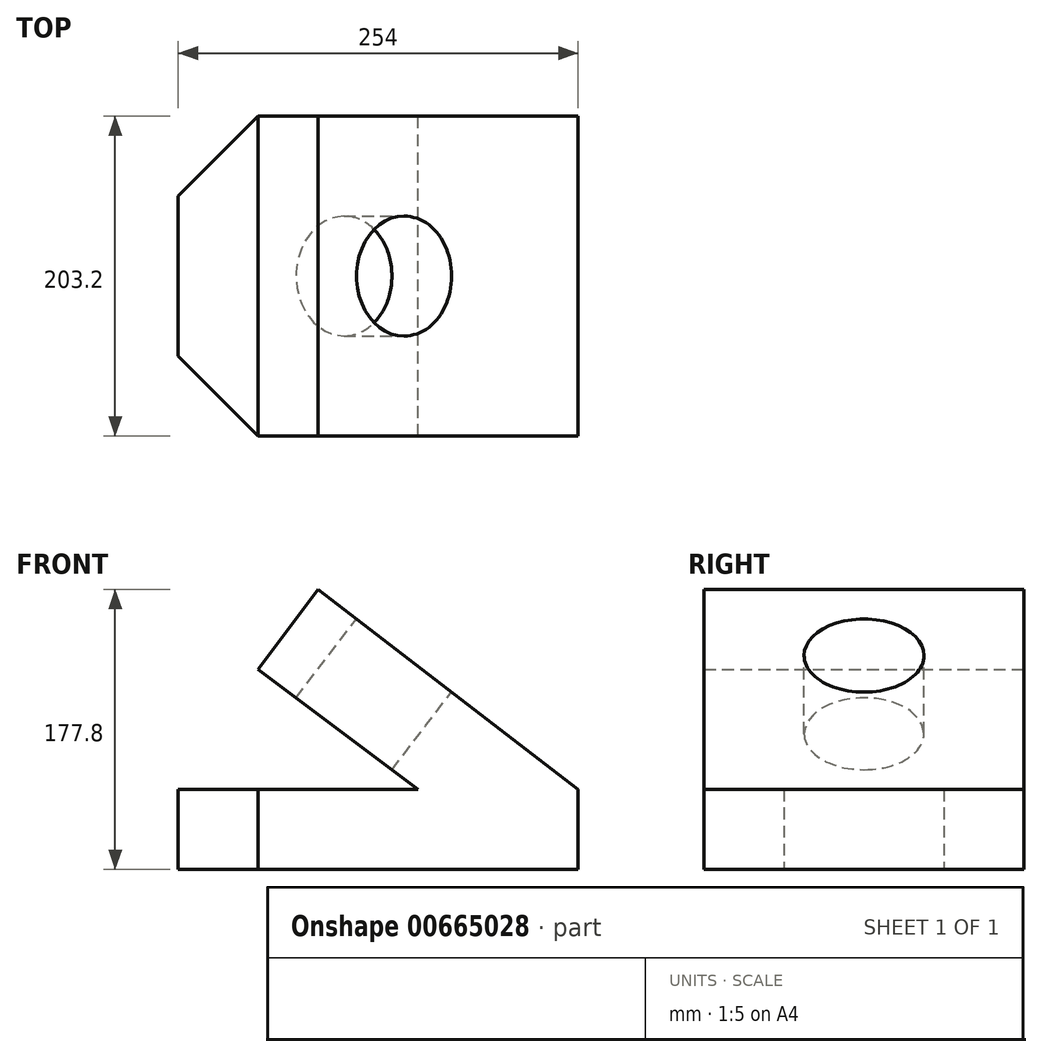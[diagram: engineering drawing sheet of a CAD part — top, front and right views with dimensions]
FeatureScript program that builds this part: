
annotation { "Feature Type Name" : "Feature", "Feature Type Description" : "" }
export const myFeature = defineFeature(function(context is Context, id is Id, definition is map)
    precondition{}
    {
        {
            var Q0;
            Q0=qCreatedBy(makeId("Front.planeOp"),FACE);
            var sketch = newSketch(context, id + "F0", { "sketchPlane" : qUnion([Q0])});
            skLineSegment(sketch, "E0", {"start": v(0, 0) * mm, "end": v(254, 0) * mm});
            skLineSegment(sketch, "E1", {"start": v(254, 0) * mm, "end": v(254, 50.8) * mm});
            skLineSegment(sketch, "E2", {"start": v(0, 0) * mm, "end": v(0, 50.8) * mm});
            skLineSegment(sketch, "E3", {"start": v(0, 50.8) * mm, "end": v(152.4, 50.8) * mm});
            skLineSegment(sketch, "E4", {"start": v(0, 50.8) * mm, "end": v(76.2, 50.8) * mm});
            skLineSegment(sketch, "E5", {"start": v(50.8, 127) * mm, "end": v(152.4, 50.8) * mm});
            skLineSegment(sketch, "E6", {"start": v(50.8, 127) * mm, "end": v(88.9, 177.8) * mm});
            skLineSegment(sketch, "E7", {"start": v(88.9, 177.8) * mm, "end": v(254, 50.8) * mm});
            skSolve(sketch);
        }
        {
            var Q0;
            Q0=makeQuery(id+"F0.imprint","IMPRINT",FACE,{"disambiguationData":[TD([[makeQuery(id+"F0.imprint","IMPRINT",EDGE,{"derivedFrom":sQuery(id+"F0.wireOp",EDGE,"E0")}),1.0]])]});
            extrude(context, id + "F1", {"entities" : qUnion([Q0]), "endBound" : BoundingType.SYMMETRIC, "depth" : 203.2 * mm, "offsetDistance" : 25.4 * mm});
        }
        {
            var Q0;
            Q0=makeQuery(id+"F1.opExtrude","SWEPT_FACE",FACE,{"disambiguationData":[OSD([sQuery(id+"F0.wireOp",EDGE,"E7")])]});
            var sketch = newSketch(context, id + "F2", { "sketchPlane" : qUnion([Q0])});
            skCircle(sketch, "E8", {"center": v(30.88, 0) * mm, "radius": 38.1 * mm});
            skSolve(sketch);
        }
        {
            var Q0;
            Q0=makeQuery(id+"F2.imprint","IMPRINT",FACE,{"disambiguationData":[TD([[makeQuery(id+"F2.imprint","IMPRINT",EDGE,{"derivedFrom":sQuery(id+"F2.wireOp",EDGE,"E8")}),1.0]])]});
            extrude(context, id + "F3", {"entities" : qUnion([Q0]), "operationType" : NewBodyOperationType.REMOVE, "oppositeDirection" : true, "depth" : 74.42 * mm, "offsetDistance" : 25.4 * mm});
        }
        {
            var Q0;
            Q0=makeQuery(id+"F1.opExtrude","SWEPT_FACE",FACE,{"disambiguationData":[OSD([sQuery(id+"F0.wireOp",EDGE,"E0")])]});
            var sketch = newSketch(context, id + "F4", { "sketchPlane" : qUnion([Q0])});
            skLineSegment(sketch, "E9", {"start": v(0, -101.6) * mm, "end": v(0, -50.8) * mm});
            skLineSegment(sketch, "E10", {"start": v(0, -101.6) * mm, "end": v(50.8, -101.6) * mm});
            skLineSegment(sketch, "E11", {"start": v(50.8, -101.6) * mm, "end": v(0, -50.8) * mm});
            skLineSegment(sketch, "E12", {"start": v(0, 101.6) * mm, "end": v(0, 50.8) * mm});
            skLineSegment(sketch, "E13", {"start": v(0, 101.6) * mm, "end": v(50.8, 101.6) * mm});
            skLineSegment(sketch, "E14", {"start": v(50.8, 101.6) * mm, "end": v(0, 50.8) * mm});
            skSolve(sketch);
        }
        {
            var Q0;
            Q0=makeQuery(id+"F4.imprint","IMPRINT",FACE,{"disambiguationData":[TD([[makeQuery(id+"F4.imprint","IMPRINT",EDGE,{"derivedFrom":sQuery(id+"F4.wireOp",EDGE,"E9")}),1.0]])]});
            var Q1;
            Q1=makeQuery(id+"F4.imprint","IMPRINT",FACE,{"disambiguationData":[TD([[makeQuery(id+"F4.imprint","IMPRINT",EDGE,{"derivedFrom":sQuery(id+"F4.wireOp",EDGE,"E12")}),1.0]])]});
            extrude(context, id + "F5", {"entities" : qUnion([Q0, Q1]), "operationType" : NewBodyOperationType.REMOVE, "oppositeDirection" : true, "depth" : 72.14 * mm, "offsetDistance" : 25.4 * mm});
        }
    });
